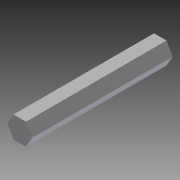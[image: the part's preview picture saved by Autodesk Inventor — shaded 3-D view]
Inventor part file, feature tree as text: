
AUTODESK INVENTOR PART (.ipt)
format: ipt  version: 2014 (Build 180170000, 170)  size: 86,016 bytes
history: native  units: in
note: dims shown in document units (in); Inventor stores cm internally (conversion verified against a paired STEP export)
features: extrude x1, sketch x1
ambient origin geometry x8: Origin, YZ Plane, XZ Plane, XY Plane, X Axis, Y Axis, Z Axis, Center Point
bodies: Solid1 (feature_tree)
feature tree (2):
  extrude  "Extrusion1"  Depth=3.25in TaperAngle=0.0deg
  sketch  "Sketch1"  dims[d0=0.5in d1=3.25in d2=0.0in]
